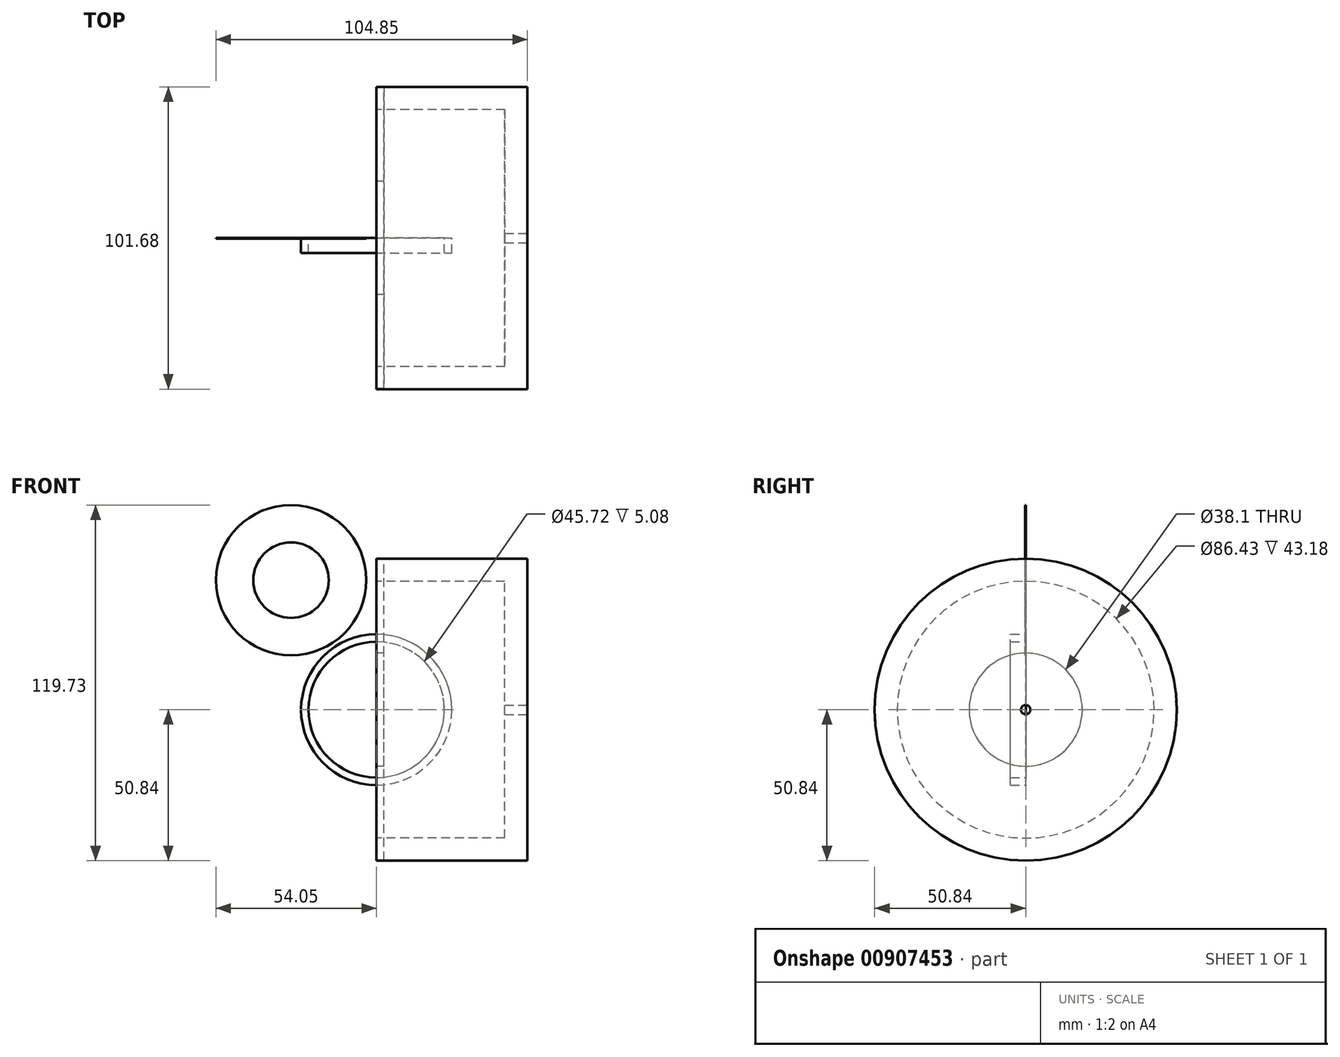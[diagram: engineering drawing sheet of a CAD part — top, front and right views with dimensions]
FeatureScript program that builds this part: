
annotation { "Feature Type Name" : "Feature", "Feature Type Description" : "" }
export const myFeature = defineFeature(function(context is Context, id is Id, definition is map)
    precondition{}
    {
        {
            var Q0;
            Q0=qCreatedBy(makeId("Right.planeOp"),FACE);
            var sketch = newSketch(context, id + "F0", { "sketchPlane" : qUnion([Q0])});
            skCircle(sketch, "E0", {"center": v(0, 0) * mm, "radius": 50.84 * mm});
            skPoint(sketch, "E1", {"position": v(96.74, 96.21) * mm});
            skSolve(sketch);
        }
        {
            var Q0;
            Q0=makeQuery(id+"F0.imprint","IMPRINT",FACE,{"disambiguationData":[TD([[makeQuery(id+"F0.imprint","IMPRINT",EDGE,{"derivedFrom":sQuery(id+"F0.wireOp",EDGE,"E0")}),1.0]])]});
            extrude(context, id + "F1", {"entities" : qUnion([Q0]), "depth" : 50.8 * mm, "offsetDistance" : 25.4 * mm});
        }
        {
            var Q0;
            Q0=makeQuery(id+"F1.opExtrude","CAP_FACE",FACE,{"disambiguationData":[OSD([sQuery(id+"F0.wireOp",EDGE,"E0")])],"isStart":true});
            shell(context, id + "F2", {"entities" : qUnion([Q0]), "thickness" : 7.62 * mm});
        }
        {
            var Q0;
            Q0=qCreatedBy(makeId("Front.planeOp"),FACE);
            var sketch = newSketch(context, id + "F3", { "sketchPlane" : qUnion([Q0])});
            skCircle(sketch, "E2", {"center": v(0, 0) * mm, "radius": 25.37 * mm});
            skSolve(sketch);
        }
        {
            var Q0;
            Q0 = qSketchRegion(id + "F3", true);
            extrude(context, id + "F4", {"entities" : qUnion([Q0]), "depth" : 5.08 * mm, "offsetDistance" : 25.4 * mm});
        }
        {
            var Q0;
            Q0=makeQuery(id+"F4.opExtrude","CAP_FACE",FACE,{"disambiguationData":[OSD([sQuery(id+"F3.wireOp",EDGE,"E2")])],"isStart":true});
            var sketch = newSketch(context, id + "F5", { "sketchPlane" : qUnion([Q0])});
            skCircle(sketch, "E3", {"center": v(0, 0) * mm, "radius": 22.98 * mm});
            skSolve(sketch);
        }
        {
            var Q0;
            Q0=sQuery(id+"F5.wireOp",VERTEX,"E3.center");
            var Q1;
            Q1=makeQuery(id+"F4.opExtrude","SWEPT_BODY",BODY,{"disambiguationData":[OSD([sQuery(id+"F3.wireOp",EDGE,"E2")])]});
            hole(context, id + "F6", {"style" : HoleStyle.SIMPLE, "endStyle" : HoleEndStyle.THROUGH, "holeDiameter" : 45.72 * mm, "majorDiameter" : 6.35 * mm, "isTappedThrough" : true, "tappedDepth" : 12.7 * mm, "tapClearance" : 3, "locations" : qUnion([Q0]), "scope" : qUnion([Q1])});
        }
        {
            var Q0;
            Q0=qCreatedBy(makeId("Front.planeOp"),FACE);
            var sketch = newSketch(context, id + "F7", { "sketchPlane" : qUnion([Q0])});
            skCircle(sketch, "E4", {"center": v(0, 0) * mm, "radius": 25.37 * mm});
            skPoint(sketch, "E5", {"position": v(0, -3.17) * mm});
            skSolve(sketch);
        }
        {
            var Q0;
            Q0 = qSketchRegion(id + "F7", true);
            extrude(context, id + "F8", {"entities" : qUnion([Q0]), "oppositeDirection" : true, "depth" : 1.27 * mm, "offsetDistance" : 25.4 * mm});
        }
        {
            var Q0;
            Q0=qCreatedBy(makeId("Front.planeOp"),FACE);
            var sketch = newSketch(context, id + "F9", { "sketchPlane" : qUnion([Q0])});
            skCircle(sketch, "E6", {"center": v(-28.74, 43.59) * mm, "radius": 25.3 * mm});
            skPoint(sketch, "E7", {"position": v(-27.64, 43.59) * mm});
            skSolve(sketch);
        }
        {
            var Q0;
            Q0 = qSketchRegion(id + "F9", true);
            extrude(context, id + "F10", {"entities" : qUnion([Q0]), "depth" : 0.25 * mm, "offsetDistance" : 25.4 * mm});
        }
        {
            var Q0;
            Q0=sQuery(id+"F9.wireOp",VERTEX,"E6.center");
            var Q1;
            Q1=makeQuery(id+"F10.opExtrude","SWEPT_BODY",BODY,{"disambiguationData":[OSD([sQuery(id+"F9.wireOp",EDGE,"E6")])]});
            hole(context, id + "F11", {"style" : HoleStyle.SIMPLE, "endStyle" : HoleEndStyle.THROUGH, "oppositeDirection" : true, "holeDiameter" : 25.4 * mm, "majorDiameter" : 6.35 * mm, "isTappedThrough" : true, "tappedDepth" : 12.7 * mm, "tapClearance" : 3, "locations" : qUnion([Q0]), "scope" : qUnion([Q1])});
        }
        {
            var Q0;
            Q0=qCreatedBy(makeId("Right.planeOp"),FACE);
            var sketch = newSketch(context, id + "F12", { "sketchPlane" : qUnion([Q0])});
            skCircle(sketch, "E8", {"center": v(0, 0) * mm, "radius": 50.7 * mm});
            skPoint(sketch, "E9", {"position": v(-3.44, 0) * mm});
            skPoint(sketch, "E10", {"position": v(2.75, -2.2) * mm});
            skPoint(sketch, "E11", {"position": v(0, 2.38) * mm});
            skSolve(sketch);
        }
        {
            var Q0;
            Q0 = qSketchRegion(id + "F12", true);
            extrude(context, id + "F13", {"entities" : qUnion([Q0]), "depth" : 2.54 * mm, "offsetDistance" : 25.4 * mm});
        }
        {
            var Q0;
            Q0=sQuery(id+"F12.wireOp",VERTEX,"E8.center");
            var Q1;
            Q1=makeQuery(id+"F13.opExtrude","SWEPT_BODY",BODY,{"disambiguationData":[OSD([sQuery(id+"F12.wireOp",EDGE,"E8")])]});
            hole(context, id + "F14", {"style" : HoleStyle.SIMPLE, "endStyle" : HoleEndStyle.THROUGH, "oppositeDirection" : true, "holeDiameter" : 38.1 * mm, "majorDiameter" : 6.35 * mm, "isTappedThrough" : true, "tappedDepth" : 12.7 * mm, "tapClearance" : 3, "locations" : qUnion([Q0]), "scope" : qUnion([Q1])});
        }
        {
            var Q0;
            Q0=makeQuery(id+"F8.opExtrude","SWEPT_BODY",BODY,{"disambiguationData":[OSD([sQuery(id+"F7.wireOp",EDGE,"E4")])]});
            deleteBodies(context, id + "F15", {"entities" : qUnion([Q0])});
        }
        {
            var Q0;
            Q0=makeQuery(id+"F1.opExtrude","CAP_FACE",FACE,{"disambiguationData":[OSD([sQuery(id+"F0.wireOp",EDGE,"E0")])],"isStart":false});
            var sketch = newSketch(context, id + "F16", { "sketchPlane" : qUnion([Q0])});
            skSolve(sketch);
        }
        {
            var Q0;
            Q0=makeQuery(id+"F16.imprint","IMPRINT",FACE,{"disambiguationData":[TD([[makeQuery(id+"F16.imprint","IMPRINT",EDGE,{"derivedFrom":makeQuery(id+"F1.opExtrude","CAP_EDGE",EDGE,{"disambiguationData":[OSD([sQuery(id+"F0.wireOp",EDGE,"E0")])],"isStart":false})}),1.0]])]});
            var sketch = newSketch(context, id + "F17", { "sketchPlane" : qUnion([Q0])});
            skSolve(sketch);
        }
        {
            var Q0;
            Q0=makeQuery(id+"F17.imprint","IMPRINT",FACE,{"disambiguationData":[TD([[makeQuery(id+"F17.imprint","IMPRINT",EDGE,{"derivedFrom":makeQuery(id+"F16.imprint","IMPRINT",EDGE,{"derivedFrom":makeQuery(id+"F1.opExtrude","CAP_EDGE",EDGE,{"disambiguationData":[OSD([sQuery(id+"F0.wireOp",EDGE,"E0")])],"isStart":false})})}),1.0]])]});
            var sketch = newSketch(context, id + "F18", { "sketchPlane" : qUnion([Q0])});
            skPoint(sketch, "E12", {"position": v(0, 0) * mm});
            skPoint(sketch, "E13", {"position": v(0, -4.29) * mm});
            skPoint(sketch, "E14", {"position": v(-23.9, 0) * mm});
            skPoint(sketch, "E15", {"position": v(-23.58, 0.16) * mm});
            skPoint(sketch, "E16", {"position": v(-22.47, 0) * mm});
            skPoint(sketch, "E17", {"position": v(-21.83, -0.16) * mm});
            skPoint(sketch, "E18", {"position": v(-20.88, -0.16) * mm});
            skPoint(sketch, "E19", {"position": v(136.48, 5.24) * mm});
            skSolve(sketch);
        }
        {
            var Q0;
            Q0=sQuery(id+"F18.wireOp",VERTEX,"E12");
            var Q1;
            Q1=makeQuery(id+"F1.opExtrude","SWEPT_BODY",BODY,{"disambiguationData":[OSD([sQuery(id+"F0.wireOp",EDGE,"E0")])]});
            hole(context, id + "F19", {"style" : HoleStyle.SIMPLE, "endStyle" : HoleEndStyle.THROUGH, "holeDiameter" : 3.17 * mm, "majorDiameter" : 6.35 * mm, "isTappedThrough" : true, "tappedDepth" : 12.7 * mm, "tapClearance" : 3, "locations" : qUnion([Q0]), "scope" : qUnion([Q1])});
        }
    });
